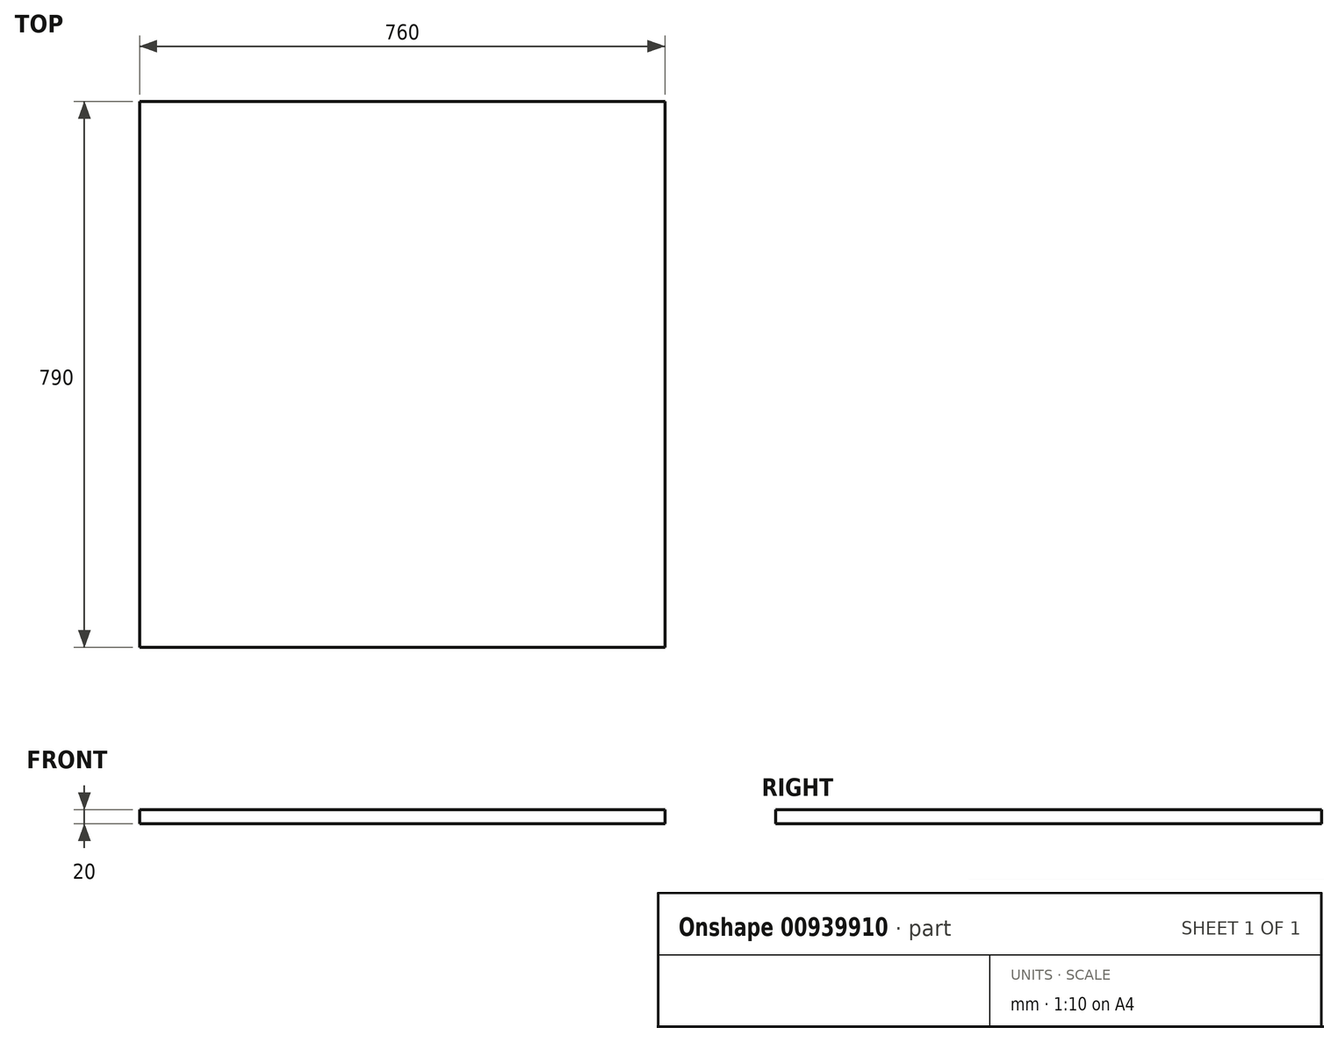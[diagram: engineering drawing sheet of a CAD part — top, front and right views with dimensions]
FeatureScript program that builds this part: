
annotation { "Feature Type Name" : "Feature", "Feature Type Description" : "" }
export const myFeature = defineFeature(function(context is Context, id is Id, definition is map)
    precondition{}
    {
        {
            var Q0;
            Q0=qCreatedBy(makeId("Top.planeOp"),FACE);
            var sketch = newSketch(context, id + "F0", { "sketchPlane" : qUnion([Q0])});
            skLineSegment(sketch, "E0.bottom", {"start": v(-60.22, 751.97) * mm, "end": v(699.78, 751.97) * mm});
            skLineSegment(sketch, "E0.top", {"start": v(-60.22, -38.03) * mm, "end": v(699.78, -38.03) * mm});
            skLineSegment(sketch, "E0.left", {"start": v(-60.22, 751.97) * mm, "end": v(-60.22, -38.03) * mm});
            skLineSegment(sketch, "E0.right", {"start": v(699.78, 751.97) * mm, "end": v(699.78, -38.03) * mm});
            skSolve(sketch);
        }
        {
            var Q0;
            Q0 = qSketchRegion(id + "F0", true);
            extrude(context, id + "F1", {"entities" : qUnion([Q0]), "depth" : 20 * mm, "offsetDistance" : 25 * mm});
        }
    });
